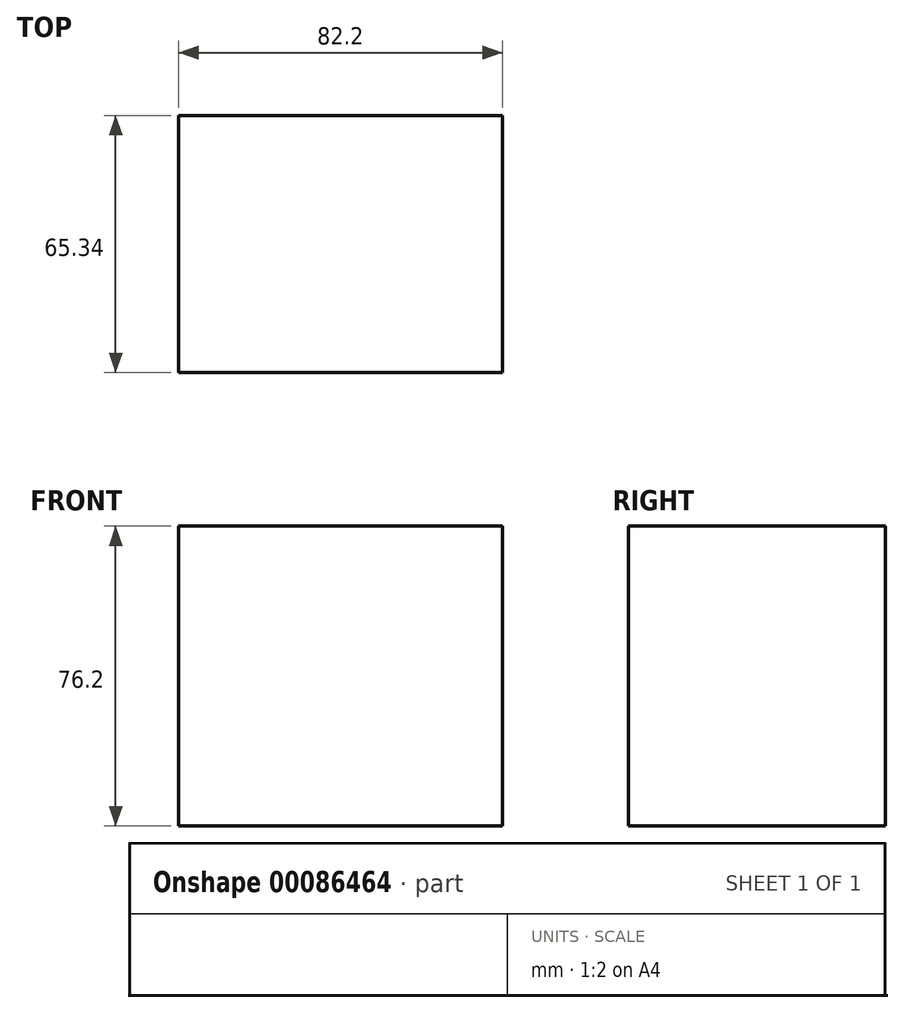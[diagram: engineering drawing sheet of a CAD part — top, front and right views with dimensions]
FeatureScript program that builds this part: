
annotation { "Feature Type Name" : "Feature", "Feature Type Description" : "" }
export const myFeature = defineFeature(function(context is Context, id is Id, definition is map)
    precondition{}
    {
        {
            var Q0;
            Q0=qCreatedBy(makeId("Top.planeOp"),FACE);
            var sketch = newSketch(context, id + "F0", { "sketchPlane" : qUnion([Q0])});
            skLineSegment(sketch, "E0.bottom", {"start": v(41.1, 32.67) * mm, "end": v(-41.1, 32.67) * mm});
            skLineSegment(sketch, "E0.top", {"start": v(41.1, -32.67) * mm, "end": v(-41.1, -32.67) * mm});
            skLineSegment(sketch, "E0.left", {"start": v(41.1, 32.67) * mm, "end": v(41.1, -32.67) * mm});
            skLineSegment(sketch, "E0.right", {"start": v(-41.1, 32.67) * mm, "end": v(-41.1, -32.67) * mm});
            skPoint(sketch, "E0.middle", {"position": v(0, 0) * mm});
            skSolve(sketch);
        }
        {
            var Q0;
            Q0=makeQuery(id+"F0.imprint","IMPRINT",FACE,{"disambiguationData":[TD([[makeQuery(id+"F0.imprint","IMPRINT",EDGE,{"derivedFrom":sQuery(id+"F0.wireOp",EDGE,"E0.bottom")}),1.0]])]});
            extrude(context, id + "F1", {"entities" : qUnion([Q0]), "depth" : 76.2 * mm});
        }
    });
